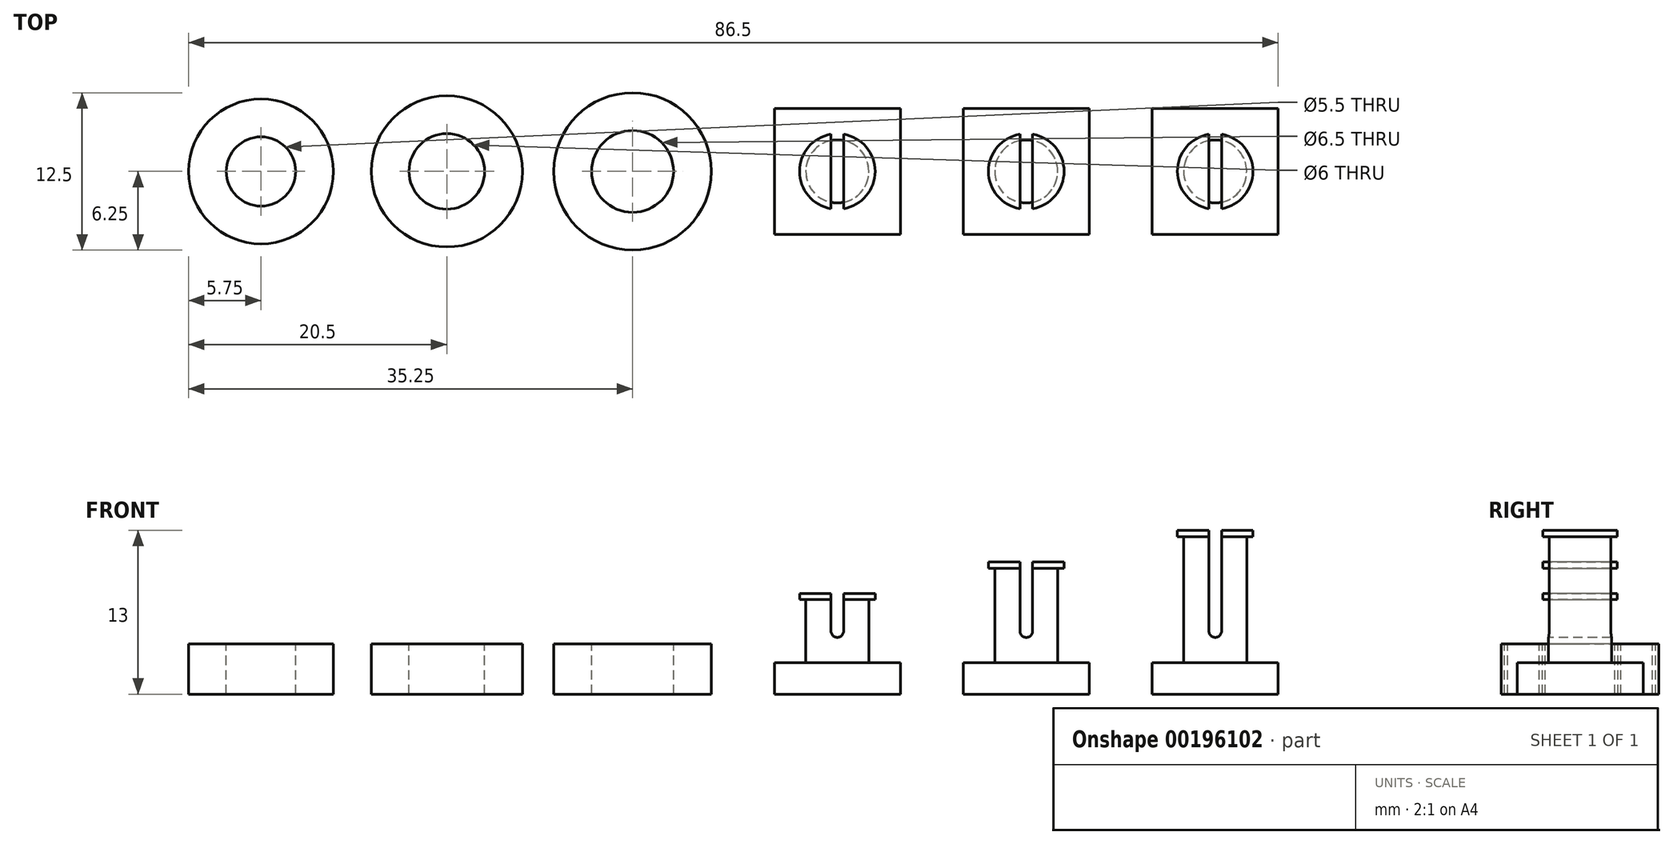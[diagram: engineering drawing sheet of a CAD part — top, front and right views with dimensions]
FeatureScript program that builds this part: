
annotation { "Feature Type Name" : "Feature", "Feature Type Description" : "" }
export const myFeature = defineFeature(function(context is Context, id is Id, definition is map)
    precondition{}
    {
        {
            var Q0;
            Q0=qCreatedBy(makeId("Front.planeOp"),FACE);
            var sketch = newSketch(context, id + "F0", { "sketchPlane" : qUnion([Q0])});
            skLineSegment(sketch, "E0", {"start": v(0, 0) * mm, "end": v(0, 16.22) * mm, "construction": true});
            skLineSegment(sketch, "E1", {"start": v(0, 8) * mm, "end": v(3, 8) * mm});
            skLineSegment(sketch, "E2", {"start": v(3, 8) * mm, "end": v(3, 7.5) * mm});
            skLineSegment(sketch, "E3", {"start": v(3, 7.5) * mm, "end": v(2.5, 7.5) * mm});
            skLineSegment(sketch, "E4", {"start": v(2.5, 7.5) * mm, "end": v(2.5, 2.5) * mm});
            skLineSegment(sketch, "E5", {"start": v(2.5, 2.5) * mm, "end": v(5, 2.5) * mm});
            skLineSegment(sketch, "E6", {"start": v(5, 2.5) * mm, "end": v(5, 0) * mm});
            skLineSegment(sketch, "E7", {"start": v(5, 0) * mm, "end": v(0, 0) * mm});
            skLineSegment(sketch, "E8", {"start": v(0, 8) * mm, "end": v(0, 0) * mm});
            skLineSegment(sketch, "E9", {"start": v(15, 0) * mm, "end": v(15, 15.04) * mm, "construction": true});
            skLineSegment(sketch, "E10", {"start": v(15, 10.5) * mm, "end": v(18, 10.5) * mm});
            skLineSegment(sketch, "E11", {"start": v(18, 10.5) * mm, "end": v(18, 10) * mm});
            skLineSegment(sketch, "E12", {"start": v(18, 10) * mm, "end": v(17.5, 10) * mm});
            skLineSegment(sketch, "E13", {"start": v(17.5, 10) * mm, "end": v(17.5, 2.5) * mm});
            skLineSegment(sketch, "E14", {"start": v(17.5, 2.5) * mm, "end": v(20, 2.5) * mm});
            skLineSegment(sketch, "E15", {"start": v(20, 2.5) * mm, "end": v(20, 0) * mm});
            skLineSegment(sketch, "E16", {"start": v(20, 0) * mm, "end": v(15, 0) * mm});
            skLineSegment(sketch, "E17", {"start": v(15, 10.5) * mm, "end": v(15, 0) * mm});
            skLineSegment(sketch, "E18", {"start": v(30, 0) * mm, "end": v(30, 27.9) * mm, "construction": true});
            skLineSegment(sketch, "E19", {"start": v(30, 13) * mm, "end": v(33, 13) * mm});
            skLineSegment(sketch, "E20", {"start": v(33, 13) * mm, "end": v(33, 12.5) * mm});
            skLineSegment(sketch, "E21", {"start": v(33, 12.5) * mm, "end": v(32.5, 12.5) * mm});
            skLineSegment(sketch, "E22", {"start": v(32.5, 12.5) * mm, "end": v(32.5, 2.5) * mm});
            skLineSegment(sketch, "E23", {"start": v(32.5, 2.5) * mm, "end": v(35, 2.5) * mm});
            skLineSegment(sketch, "E24", {"start": v(35, 2.5) * mm, "end": v(35, 0) * mm});
            skLineSegment(sketch, "E25", {"start": v(35, 0) * mm, "end": v(30, 0) * mm});
            skLineSegment(sketch, "E26", {"start": v(30, 13) * mm, "end": v(30, 0) * mm});
            skSolve(sketch);
        }
        {
            var Q0;
            Q0=makeQuery(id+"F0.imprint","IMPRINT",FACE,{"disambiguationData":[TD([[makeQuery(id+"F0.imprint","IMPRINT",EDGE,{"derivedFrom":sQuery(id+"F0.wireOp",EDGE,"E1")}),-1.0]])]});
            var Q1;
            Q1=sQuery(id+"F0.wireOp",EDGE,"E0");
            revolve(context, id + "F1", {"entities" : qUnion([Q0]), "axis" : qUnion([Q1]), "revolveType" : RevolveType.FULL});
        }
        {
            var Q0;
            Q0=makeQuery(id+"F0.imprint","IMPRINT",FACE,{"disambiguationData":[TD([[makeQuery(id+"F0.imprint","IMPRINT",EDGE,{"derivedFrom":sQuery(id+"F0.wireOp",EDGE,"E10")}),-1.0]])]});
            var Q1;
            Q1=sQuery(id+"F0.wireOp",EDGE,"E9");
            revolve(context, id + "F2", {"entities" : qUnion([Q0]), "axis" : qUnion([Q1]), "revolveType" : RevolveType.FULL});
        }
        {
            var Q0;
            Q0=makeQuery(id+"F0.imprint","IMPRINT",FACE,{"disambiguationData":[TD([[makeQuery(id+"F0.imprint","IMPRINT",EDGE,{"derivedFrom":sQuery(id+"F0.wireOp",EDGE,"E19")}),-1.0]])]});
            var Q1;
            Q1=sQuery(id+"F0.wireOp",EDGE,"E18");
            revolve(context, id + "F3", {"entities" : qUnion([Q0]), "axis" : qUnion([Q1]), "revolveType" : RevolveType.FULL});
        }
        {
            var Q0;
            Q0=qCreatedBy(makeId("Front.planeOp"),FACE);
            var sketch = newSketch(context, id + "F4", { "sketchPlane" : qUnion([Q0])});
            skLineSegment(sketch, "E27", {"start": v(0, 15.96) * mm, "end": v(0, 0) * mm, "construction": true});
            skLineSegment(sketch, "E28", {"start": v(0, 8) * mm, "end": v(0.5, 8) * mm});
            skLineSegment(sketch, "E29", {"start": v(0.5, 8) * mm, "end": v(0.5, 5) * mm});
            skLineSegment(sketch, "E30", {"start": v(0.5, 5) * mm, "end": v(0, 5) * mm, "construction": true});
            skLineSegment(sketch, "E31", {"start": v(0, 5) * mm, "end": v(0, 8) * mm});
            skArc(sketch, "E32", {"start": v(0, 4.5) * mm, "mid": v(0.35, 4.65) * mm, "end": v(0.5, 5) * mm});
            skLineSegment(sketch, "E33.MirrorCS", {"start": v(0, 8) * mm, "end": v(-0.5, 8) * mm});
            skLineSegment(sketch, "E34.MirrorCS", {"start": v(-0.5, 8) * mm, "end": v(-0.5, 5) * mm});
            skArc(sketch, "E35.MirrorCS", {"start": v(0, 4.5) * mm, "mid": v(-0.35, 4.65) * mm, "end": v(-0.5, 5) * mm});
            skLineSegment(sketch, "E36", {"start": v(15, 23.7) * mm, "end": v(15, 7.74) * mm, "construction": true});
            skLineSegment(sketch, "E37", {"start": v(15, 10.5) * mm, "end": v(15.5, 10.5) * mm});
            skLineSegment(sketch, "E38", {"start": v(15.5, 10.5) * mm, "end": v(15.5, 5) * mm});
            skLineSegment(sketch, "E39", {"start": v(15.5, 5) * mm, "end": v(15, 5) * mm, "construction": true});
            skLineSegment(sketch, "E40", {"start": v(15, 5) * mm, "end": v(15, 10.5) * mm});
            skArc(sketch, "E41", {"start": v(15, 4.5) * mm, "mid": v(15.35, 4.65) * mm, "end": v(15.5, 5) * mm});
            skLineSegment(sketch, "E42.MirrorCS", {"start": v(15, 10.5) * mm, "end": v(14.5, 10.5) * mm});
            skLineSegment(sketch, "E43.MirrorCS", {"start": v(14.5, 10.5) * mm, "end": v(14.5, 5) * mm});
            skArc(sketch, "E44.MirrorCS", {"start": v(15, 4.5) * mm, "mid": v(14.65, 4.65) * mm, "end": v(14.5, 5) * mm});
            skLineSegment(sketch, "E45", {"start": v(30, 24.52) * mm, "end": v(30, 8.56) * mm, "construction": true});
            skLineSegment(sketch, "E46", {"start": v(30, 13) * mm, "end": v(30.5, 13) * mm});
            skLineSegment(sketch, "E47", {"start": v(30.5, 13) * mm, "end": v(30.5, 5) * mm});
            skLineSegment(sketch, "E48", {"start": v(30.5, 5) * mm, "end": v(30, 5) * mm, "construction": true});
            skLineSegment(sketch, "E49", {"start": v(30, 5) * mm, "end": v(30, 13) * mm});
            skArc(sketch, "E50", {"start": v(30, 4.5) * mm, "mid": v(30.35, 4.65) * mm, "end": v(30.5, 5) * mm});
            skLineSegment(sketch, "E51.MirrorCS", {"start": v(30, 13) * mm, "end": v(29.5, 13) * mm});
            skLineSegment(sketch, "E52.MirrorCS", {"start": v(29.5, 13) * mm, "end": v(29.5, 5) * mm});
            skArc(sketch, "E53.MirrorCS", {"start": v(30, 4.5) * mm, "mid": v(29.65, 4.65) * mm, "end": v(29.5, 5) * mm});
            skSolve(sketch);
        }
        {
            var Q0;
            Q0 = qSketchRegion(id + "F4", true);
            extrude(context, id + "F5", {"entities" : qUnion([Q0]), "operationType" : NewBodyOperationType.REMOVE, "oppositeDirection" : true, "depth" : 25 * mm, "hasSecondDirection" : true, "secondDirectionOppositeDirection" : false, "secondDirectionDepth" : 25 * mm});
        }
        {
            var Q0;
            Q0=qCreatedBy(makeId("Front.planeOp"),FACE);
            var sketch = newSketch(context, id + "F6", { "sketchPlane" : qUnion([Q0])});
            skLineSegment(sketch, "E54.top", {"start": v(-16.25, 0) * mm, "end": v(-10, 0) * mm, "construction": true});
            skLineSegment(sketch, "E54.left", {"start": v(-16.25, 12.4) * mm, "end": v(-16.25, 0) * mm, "construction": true});
            skLineSegment(sketch, "E54.right", {"start": v(-10, 4) * mm, "end": v(-10, 0) * mm});
            skLineSegment(sketch, "E55", {"start": v(-10, 4) * mm, "end": v(-13, 4) * mm});
            skLineSegment(sketch, "E56", {"start": v(-10, 0) * mm, "end": v(-13, 0) * mm});
            skLineSegment(sketch, "E57", {"start": v(-13, 4) * mm, "end": v(-13, 0) * mm});
            skLineSegment(sketch, "E58.top", {"start": v(-31, 0) * mm, "end": v(-25, 0) * mm, "construction": true});
            skLineSegment(sketch, "E58.left", {"start": v(-31, 11.75) * mm, "end": v(-31, 0) * mm, "construction": true});
            skLineSegment(sketch, "E58.right", {"start": v(-25, 4) * mm, "end": v(-25, 0) * mm});
            skLineSegment(sketch, "E59", {"start": v(-25, 4) * mm, "end": v(-28, 4) * mm});
            skLineSegment(sketch, "E60", {"start": v(-25, 0) * mm, "end": v(-28, 0) * mm});
            skLineSegment(sketch, "E61", {"start": v(-28, 4) * mm, "end": v(-28, 0) * mm});
            skLineSegment(sketch, "E62.top", {"start": v(-45.75, 0) * mm, "end": v(-40, 0) * mm, "construction": true});
            skLineSegment(sketch, "E62.left", {"start": v(-45.75, 14.33) * mm, "end": v(-45.75, 0) * mm, "construction": true});
            skLineSegment(sketch, "E62.right", {"start": v(-40, 4) * mm, "end": v(-40, 0) * mm});
            skLineSegment(sketch, "E63", {"start": v(-40, 4) * mm, "end": v(-43, 4) * mm});
            skLineSegment(sketch, "E64", {"start": v(-40, 0) * mm, "end": v(-43, 0) * mm});
            skLineSegment(sketch, "E65", {"start": v(-43, 4) * mm, "end": v(-43, 0) * mm});
            skSolve(sketch);
        }
        {
            var Q0;
            Q0=makeQuery(id+"F6.imprint","IMPRINT",FACE,{"disambiguationData":[TD([[makeQuery(id+"F6.imprint","IMPRINT",EDGE,{"derivedFrom":sQuery(id+"F6.wireOp",EDGE,"E54.right")}),-1.0]])]});
            var Q1;
            Q1=sQuery(id+"F6.wireOp",EDGE,"E54.left");
            revolve(context, id + "F7", {"entities" : qUnion([Q0]), "axis" : qUnion([Q1]), "revolveType" : RevolveType.FULL});
        }
        {
            var Q0;
            Q0=makeQuery(id+"F6.imprint","IMPRINT",FACE,{"disambiguationData":[TD([[makeQuery(id+"F6.imprint","IMPRINT",EDGE,{"derivedFrom":sQuery(id+"F6.wireOp",EDGE,"E58.right")}),-1.0]])]});
            var Q1;
            Q1=sQuery(id+"F6.wireOp",EDGE,"E58.left");
            revolve(context, id + "F8", {"entities" : qUnion([Q0]), "axis" : qUnion([Q1]), "revolveType" : RevolveType.FULL});
        }
        {
            var Q0;
            Q0=makeQuery(id+"F6.imprint","IMPRINT",FACE,{"disambiguationData":[TD([[makeQuery(id+"F6.imprint","IMPRINT",EDGE,{"derivedFrom":sQuery(id+"F6.wireOp",EDGE,"E62.right")}),-1.0]])]});
            var Q1;
            Q1=sQuery(id+"F6.wireOp",EDGE,"E62.left");
            revolve(context, id + "F9", {"entities" : qUnion([Q0]), "axis" : qUnion([Q1]), "revolveType" : RevolveType.FULL});
        }
        {
            var Q0;
            Q0=makeQuery(id+"F1.opRevolve","SWEPT_FACE",FACE,{"disambiguationData":[OSD([sQuery(id+"F0.wireOp",EDGE,"E7")])]});
            var sketch = newSketch(context, id + "F10", { "sketchPlane" : qUnion([Q0])});
            skLineSegment(sketch, "E66.bottom", {"start": v(-5, 5) * mm, "end": v(5, 5) * mm});
            skLineSegment(sketch, "E66.top", {"start": v(-5, -5) * mm, "end": v(5, -5) * mm});
            skLineSegment(sketch, "E66.left", {"start": v(-5, 5) * mm, "end": v(-5, -5) * mm});
            skLineSegment(sketch, "E66.right", {"start": v(5, 5) * mm, "end": v(5, -5) * mm});
            skLineSegment(sketch, "E67.bottom", {"start": v(10, 5) * mm, "end": v(20, 5) * mm});
            skLineSegment(sketch, "E67.top", {"start": v(10, -5) * mm, "end": v(20, -5) * mm});
            skLineSegment(sketch, "E67.left", {"start": v(10, 5) * mm, "end": v(10, -5) * mm});
            skLineSegment(sketch, "E67.right", {"start": v(20, 5) * mm, "end": v(20, -5) * mm});
            skLineSegment(sketch, "E68.bottom", {"start": v(25, 5) * mm, "end": v(35, 5) * mm});
            skLineSegment(sketch, "E68.top", {"start": v(25, -5) * mm, "end": v(35, -5) * mm});
            skLineSegment(sketch, "E68.left", {"start": v(25, 5) * mm, "end": v(25, -5) * mm});
            skLineSegment(sketch, "E68.right", {"start": v(35, 5) * mm, "end": v(35, -5) * mm});
            skSolve(sketch);
        }
        {
            var Q0;
            Q0 = qSketchRegion(id + "F10", true);
            var Q1;
            Q1=makeQuery(id+"F1.opRevolve","SWEPT_FACE",FACE,{"disambiguationData":[OSD([sQuery(id+"F0.wireOp",EDGE,"E5")])]});
            extrude(context, id + "F11", {"entities" : qUnion([Q0]), "operationType" : NewBodyOperationType.ADD, "endBound" : BoundingType.UP_TO_SURFACE, "oppositeDirection" : true, "endBoundEntityFace" : qUnion([Q1]), "depth" : 25 * mm});
        }
    });
